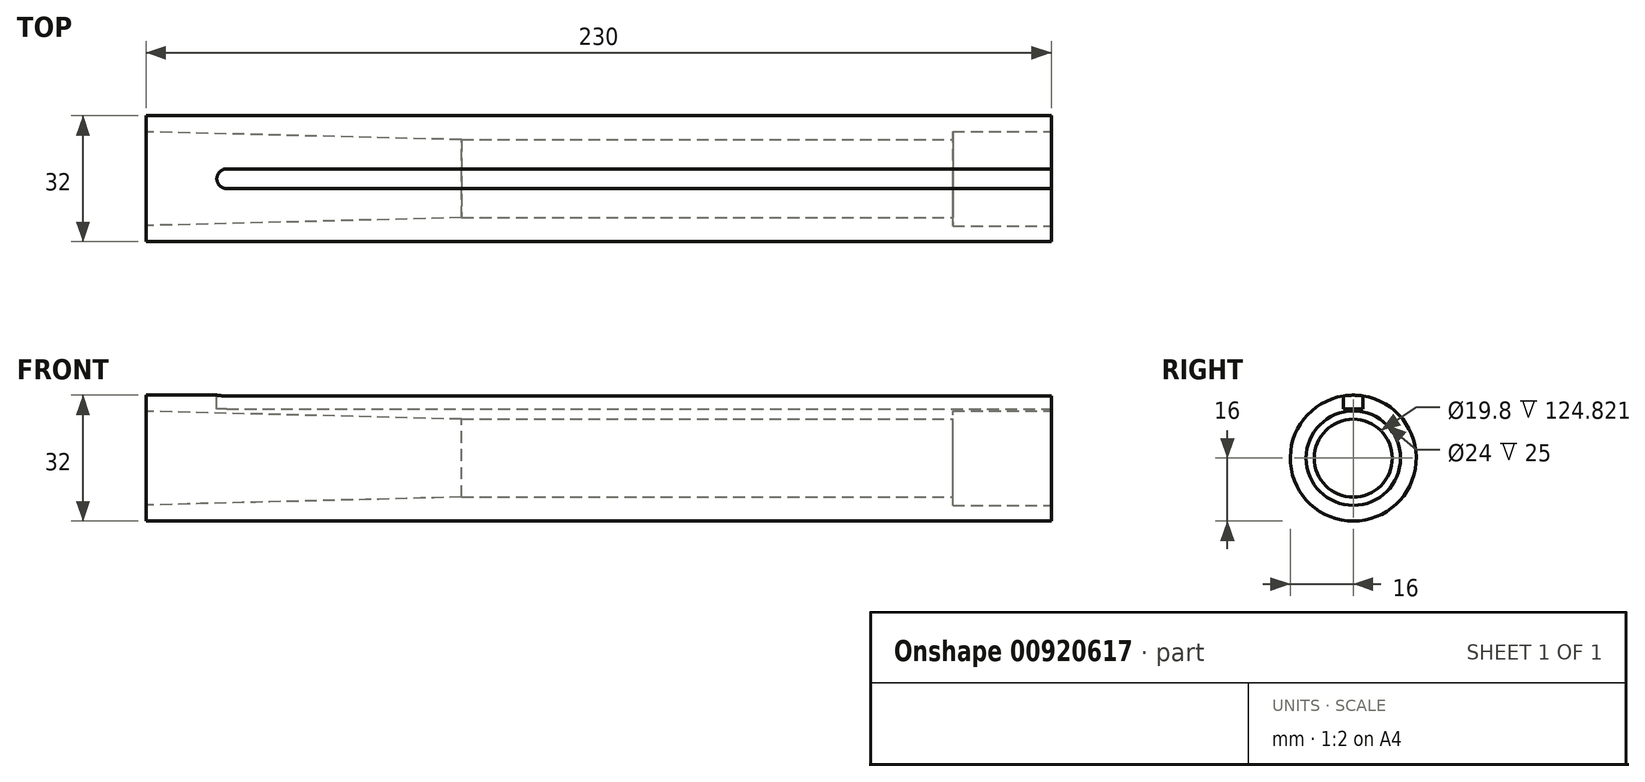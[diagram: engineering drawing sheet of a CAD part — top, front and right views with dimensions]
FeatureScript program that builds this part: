
annotation { "Feature Type Name" : "Feature", "Feature Type Description" : "" }
export const myFeature = defineFeature(function(context is Context, id is Id, definition is map)
    precondition{}
    {
        {
            var Q0;
            Q0=qCreatedBy(makeId("Front.planeOp"),FACE);
            var sketch = newSketch(context, id + "F0", { "sketchPlane" : qUnion([Q0])});
            skLineSegment(sketch, "E0", {"start": v(0, 0) * mm, "end": v(-32.5, 0) * mm, "construction": true});
            skLineSegment(sketch, "E1", {"start": v(0, 16) * mm, "end": v(-230, 16) * mm});
            skLineSegment(sketch, "E2", {"start": v(-230, 16) * mm, "end": v(-230, 11.91) * mm});
            skLineSegment(sketch, "E3", {"start": v(-230, 11.91) * mm, "end": v(-149.82, 9.9) * mm});
            skLineSegment(sketch, "E4", {"start": v(-149.82, 9.9) * mm, "end": v(-25, 9.9) * mm});
            skLineSegment(sketch, "E5", {"start": v(-229, 11.89) * mm, "end": v(-229, -11.26) * mm, "construction": true});
            skLineSegment(sketch, "E6", {"start": v(-25, 9.9) * mm, "end": v(-25, 12) * mm});
            skLineSegment(sketch, "E7", {"start": v(-25, 12) * mm, "end": v(0, 12) * mm});
            skLineSegment(sketch, "E8", {"start": v(0, 12) * mm, "end": v(0, 16) * mm});
            skSolve(sketch);
        }
        {
            var Q0;
            Q0=makeQuery(id+"F0.imprint","IMPRINT",FACE,{"disambiguationData":[TD([[makeQuery(id+"F0.imprint","IMPRINT",EDGE,{"derivedFrom":sQuery(id+"F0.wireOp",EDGE,"31kPHLTw-eswz-mXT3-GZ7P-E7lhaVrdSS14")}),1.0]])]});
            var Q1;
            Q1=makeQuery(id+"F0.imprint","IMPRINT",FACE,{"disambiguationData":[TD([[makeQuery(id+"F0.imprint","IMPRINT",EDGE,{"derivedFrom":sQuery(id+"F0.wireOp",EDGE,"E1")}),1.0]])]});
            var Q2;
            Q2=sQuery(id+"F0.wireOp",EDGE,"E0");
            revolve(context, id + "F1", {"surfaceOperationType" : NewSurfaceOperationType.NEW, "entities" : qUnion([Q0, Q1]), "axis" : qUnion([Q2]), "revolveType" : RevolveType.FULL});
        }
        {
            var Q0;
            Q0=qCreatedBy(makeId("Right.planeOp"),FACE);
            var sketch = newSketch(context, id + "F2", { "sketchPlane" : qUnion([Q0])});
            skLineSegment(sketch, "E9.bottom", {"start": v(-2.5, 16.5) * mm, "end": v(2.5, 16.5) * mm});
            skLineSegment(sketch, "E9.top", {"start": v(-2.5, 12.5) * mm, "end": v(2.5, 12.5) * mm});
            skLineSegment(sketch, "E9.left", {"start": v(-2.5, 16.5) * mm, "end": v(-2.5, 12.5) * mm});
            skLineSegment(sketch, "E9.right", {"start": v(2.5, 16.5) * mm, "end": v(2.5, 12.5) * mm});
            skSolve(sketch);
        }
        {
            var Q0;
            Q0=makeQuery(id+"F2.imprint","IMPRINT",FACE,{"disambiguationData":[TD([[makeQuery(id+"F2.imprint","IMPRINT",EDGE,{"derivedFrom":sQuery(id+"F2.wireOp",EDGE,"E9.bottom")}),-1.0]])]});
            extrude(context, id + "F3", {"entities" : qUnion([Q0]), "operationType" : NewBodyOperationType.REMOVE, "oppositeDirection" : true, "depth" : 212 * mm, "offsetDistance" : 25 * mm});
        }
        {
            var Q0;
            Q0=makeQuery(id+"F3.boolean.opBoolean","COPY",EDGE,{"derivedFrom":makeQuery(id+"F3.opExtrude","CAP_EDGE",EDGE,{"disambiguationData":[OSD([sQuery(id+"F2.wireOp",EDGE,"E9.right")])],"isStart":false})});
            var Q1;
            Q1=makeQuery(id+"F3.boolean.opBoolean","COPY",EDGE,{"derivedFrom":makeQuery(id+"F3.opExtrude","CAP_EDGE",EDGE,{"disambiguationData":[OSD([sQuery(id+"F2.wireOp",EDGE,"E9.left")])],"isStart":false})});
            fillet(context, id + "F4", {"entities" : qUnion([Q0, Q1]), "radius" : 2.5 * mm, "tangentPropagation" : true, "allowEdgeOverflow" : false});
        }
    });
